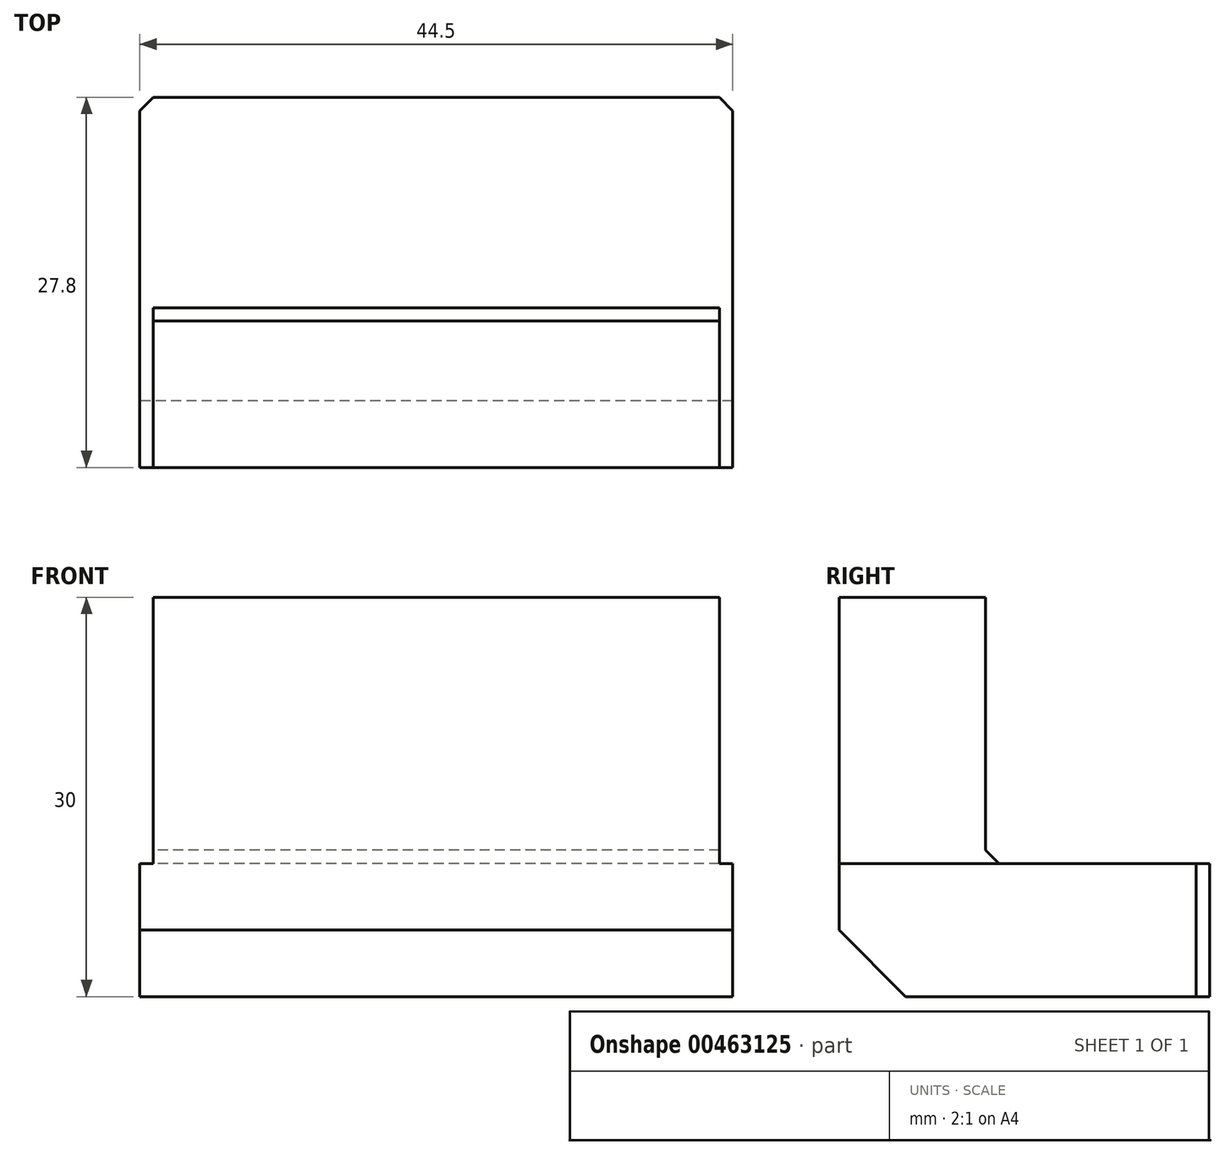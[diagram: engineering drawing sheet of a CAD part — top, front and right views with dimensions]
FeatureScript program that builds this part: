
annotation { "Feature Type Name" : "Feature", "Feature Type Description" : "" }
export const myFeature = defineFeature(function(context is Context, id is Id, definition is map)
    precondition{}
    {
        {
            var Q0;
            Q0=qCreatedBy(makeId("Top.planeOp"),FACE);
            var sketch = newSketch(context, id + "F0", { "sketchPlane" : qUnion([Q0])});
            skLineSegment(sketch, "E0.bottom", {"start": v(22.25, -13.9) * mm, "end": v(-22.25, -13.9) * mm});
            skLineSegment(sketch, "E0.top", {"start": v(22.25, 13.9) * mm, "end": v(-22.25, 13.9) * mm});
            skLineSegment(sketch, "E0.left", {"start": v(22.25, -13.9) * mm, "end": v(22.25, 13.9) * mm});
            skLineSegment(sketch, "E0.right", {"start": v(-22.25, -13.9) * mm, "end": v(-22.25, 13.9) * mm});
            skPoint(sketch, "E0.middle", {"position": v(0, 0) * mm});
            skLineSegment(sketch, "E1", {"start": v(-21.25, 13.9) * mm, "end": v(-21.25, -13.9) * mm});
            skLineSegment(sketch, "E2", {"start": v(21.25, 13.9) * mm, "end": v(21.25, -13.9) * mm});
            skLineSegment(sketch, "E3", {"start": v(-21.25, -2.9) * mm, "end": v(21.25, -2.9) * mm});
            skSolve(sketch);
        }
        {
            var Q0;
            Q0=makeQuery(id+"F0.imprint","IMPRINT",FACE,{"disambiguationData":[TD([[makeQuery(id+"F0.imprint","IMPRINT",EDGE,{"derivedFrom":sQuery(id+"F0.wireOp",EDGE,"E0.bottom")}),-1.0]])]});
            var Q1;
            {var subQ5=sQuery(id+"F0.wireOp",EDGE,"E3");Q1=makeQuery(id+"F0.imprint","IMPRINT",FACE,{"disambiguationData":[TD([[makeQuery(id+"F0.imprint","IMPRINT",EDGE,{"derivedFrom":subQ5}),1.0]])]});}
            var Q2;
            {var subQ4=sQuery(id+"F0.wireOp",EDGE,"E0.right");Q2=makeQuery(id+"F0.imprint","IMPRINT",FACE,{"disambiguationData":[TD([[makeQuery(id+"F0.imprint","IMPRINT",EDGE,{"derivedFrom":subQ4}),-1.0]])]});}
            var Q3;
            {var subQ0=sQuery(id+"F0.wireOp",EDGE,"E0.left");Q3=makeQuery(id+"F0.imprint","IMPRINT",FACE,{"disambiguationData":[TD([[makeQuery(id+"F0.imprint","IMPRINT",EDGE,{"derivedFrom":subQ0}),1.0]])]});}
            extrude(context, id + "F1", {"entities" : qUnion([Q0, Q1, Q2, Q3]), "oppositeDirection" : true, "depth" : 30 * mm});
        }
        {
            var Q0;
            {var subQ0=sQuery(id+"F0.wireOp",EDGE,"E0.right");Q0=makeQuery(id+"F0.imprint","IMPRINT",FACE,{"disambiguationData":[TD([[makeQuery(id+"F0.imprint","IMPRINT",EDGE,{"derivedFrom":subQ0}),-1.0]])]});}
            var Q1;
            {var subQ0=sQuery(id+"F0.wireOp",EDGE,"E0.left");Q1=makeQuery(id+"F0.imprint","IMPRINT",FACE,{"disambiguationData":[TD([[makeQuery(id+"F0.imprint","IMPRINT",EDGE,{"derivedFrom":subQ0}),1.0]])]});}
            extrude(context, id + "F2", {"entities" : qUnion([Q0, Q1]), "operationType" : NewBodyOperationType.REMOVE, "oppositeDirection" : true, "depth" : 20 * mm});
        }
        {
            var Q0;
            {var subQ5=sQuery(id+"F0.wireOp",EDGE,"E3");Q0=makeQuery(id+"F0.imprint","IMPRINT",FACE,{"disambiguationData":[TD([[makeQuery(id+"F0.imprint","IMPRINT",EDGE,{"derivedFrom":subQ5}),1.0]])]});}
            extrude(context, id + "F3", {"entities" : qUnion([Q0]), "operationType" : NewBodyOperationType.REMOVE, "oppositeDirection" : true, "depth" : 20 * mm});
        }
        {
            var Q0;
            Q0=makeQuery(id+"F1.opExtrude","CAP_EDGE",EDGE,{"disambiguationData":[OSD([sQuery(id+"F0.wireOp",EDGE,"E0.bottom")])],"isStart":false});
            var Q1;
            {var subQ0=sQuery(id+"F0.wireOp",EDGE,"E0.top");Q1=makeQuery(id+"F3.boolean.opBoolean","MERGE",EDGE,{"derivedFrom":[makeQuery(id+"F2.boolean.opBoolean","COPY",EDGE,{"derivedFrom":makeQuery(id+"F2.opExtrude","CAP_EDGE",EDGE,{"disambiguationData":[OSD([subQ0]),TDD([makeQuery(id+"F0.imprint","IMPRINT",EDGE,{"disambiguationData":[TD([[makeQuery(id+"F0.imprint","INTERSECT",VERTEX,{"derivedFrom":[subQ0,sQuery(id+"F0.wireOp",EDGE,"E0.left")]}),-1.0]])],"derivedFrom":subQ0})])],"isStart":false})}),makeQuery(id+"F2.boolean.opBoolean","COPY",EDGE,{"derivedFrom":makeQuery(id+"F2.opExtrude","CAP_EDGE",EDGE,{"disambiguationData":[OSD([subQ0]),TDD([makeQuery(id+"F0.imprint","IMPRINT",EDGE,{"disambiguationData":[TD([[makeQuery(id+"F0.imprint","INTERSECT",VERTEX,{"derivedFrom":[subQ0,sQuery(id+"F0.wireOp",EDGE,"E0.right")]}),1.0]])],"derivedFrom":subQ0})])],"isStart":false})}),makeQuery(id+"F3.opExtrude","CAP_EDGE",EDGE,{"disambiguationData":[OSD([subQ0])],"isStart":false})]});}
            chamfer(context, id + "F4", {"entities" : qUnion([Q0, Q1]), "width" : 5 * mm, "tangentPropagation" : true});
        }
        {
            var Q0;
            {var subQ0=sQuery(id+"F0.wireOp",EDGE,"E0.bottom");Q0=makeQuery(id+"F2.boolean.opBoolean","COPY",EDGE,{"derivedFrom":makeQuery(id+"F2.opExtrude","CAP_EDGE",EDGE,{"disambiguationData":[OSD([subQ0]),TDD([makeQuery(id+"F0.imprint","IMPRINT",EDGE,{"disambiguationData":[TD([[makeQuery(id+"F0.imprint","INTERSECT",VERTEX,{"derivedFrom":[subQ0,sQuery(id+"F0.wireOp",EDGE,"E0.right")]}),1.0]])],"derivedFrom":subQ0})])],"isStart":false})});}
            var Q1;
            {var subQ0=sQuery(id+"F0.wireOp",EDGE,"E0.bottom");Q1=makeQuery(id+"F2.boolean.opBoolean","COPY",EDGE,{"derivedFrom":makeQuery(id+"F2.opExtrude","CAP_EDGE",EDGE,{"disambiguationData":[OSD([subQ0]),TDD([makeQuery(id+"F0.imprint","IMPRINT",EDGE,{"disambiguationData":[TD([[makeQuery(id+"F0.imprint","INTERSECT",VERTEX,{"derivedFrom":[subQ0,sQuery(id+"F0.wireOp",EDGE,"E0.left")]}),-1.0]])],"derivedFrom":subQ0})])],"isStart":false})});}
            var Q2;
            Q2=makeQuery(id+"F3.boolean.opBoolean","COPY",EDGE,{"derivedFrom":makeQuery(id+"F3.opExtrude","CAP_EDGE",EDGE,{"disambiguationData":[OSD([sQuery(id+"F0.wireOp",EDGE,"E3")])],"isStart":false})});
            var Q3;
            Q3=makeQuery(id+"F2.boolean.opBoolean","COPY",EDGE,{"derivedFrom":makeQuery(id+"F2.opExtrude","SWEPT_EDGE",EDGE,{"disambiguationData":[OSD([sQuery(id+"F0.wireOp",EDGE,"E0.bottom"),sQuery(id+"F0.wireOp",EDGE,"E1")])]})});
            var Q4;
            Q4=makeQuery(id+"F2.boolean.opBoolean","COPY",EDGE,{"derivedFrom":makeQuery(id+"F2.opExtrude","SWEPT_EDGE",EDGE,{"disambiguationData":[OSD([sQuery(id+"F0.wireOp",EDGE,"E0.bottom"),sQuery(id+"F0.wireOp",EDGE,"E2")])]})});
            var Q5;
            Q5=makeQuery(id+"F3.boolean.opBoolean","COPY",EDGE,{"derivedFrom":makeQuery(id+"F3.opExtrude","SWEPT_EDGE",EDGE,{"disambiguationData":[OSD([sQuery(id+"F0.wireOp",EDGE,"E2"),sQuery(id+"F0.wireOp",EDGE,"E3")])]})});
            var Q6;
            Q6=makeQuery(id+"F3.boolean.opBoolean","COPY",EDGE,{"derivedFrom":makeQuery(id+"F3.opExtrude","SWEPT_EDGE",EDGE,{"disambiguationData":[OSD([sQuery(id+"F0.wireOp",EDGE,"E1"),sQuery(id+"F0.wireOp",EDGE,"E3")])]})});
            var Q7;
            Q7=makeQuery(id+"F1.opExtrude","SWEPT_EDGE",EDGE,{"disambiguationData":[OSD([sQuery(id+"F0.wireOp",EDGE,"E0.top"),sQuery(id+"F0.wireOp",EDGE,"E0.right")])]});
            var Q8;
            Q8=makeQuery(id+"F1.opExtrude","SWEPT_EDGE",EDGE,{"disambiguationData":[OSD([sQuery(id+"F0.wireOp",EDGE,"E0.top"),sQuery(id+"F0.wireOp",EDGE,"E0.left")])]});
            var Q9;
            {var subQ0=sQuery(id+"F0.wireOp",EDGE,"E2");var subQ1=sQuery(id+"F0.wireOp",EDGE,"E1");var subQ2=sQuery(id+"F0.wireOp",EDGE,"E0.top");var subQ3=sQuery(id+"F0.wireOp",EDGE,"E0.right");var subQ4=sQuery(id+"F0.wireOp",EDGE,"E0.bottom");var subQ5=sQuery(id+"F0.wireOp",EDGE,"E0.left");Q9=makeQuery(id+"F4.opChamfer","BLEND_EDGE",EDGE,{"blendedFrom":[makeQuery(id+"F3.boolean.opBoolean","MERGE",EDGE,{"derivedFrom":[makeQuery(id+"F2.boolean.opBoolean","COPY",EDGE,{"derivedFrom":makeQuery(id+"F2.opExtrude","CAP_EDGE",EDGE,{"disambiguationData":[OSD([subQ2]),TDD([makeQuery(id+"F0.imprint","IMPRINT",EDGE,{"disambiguationData":[TD([[makeQuery(id+"F0.imprint","INTERSECT",VERTEX,{"derivedFrom":[subQ2,subQ5]}),-1.0]])],"derivedFrom":subQ2})])],"isStart":false})}),makeQuery(id+"F2.boolean.opBoolean","COPY",EDGE,{"derivedFrom":makeQuery(id+"F2.opExtrude","CAP_EDGE",EDGE,{"disambiguationData":[OSD([subQ2]),TDD([makeQuery(id+"F0.imprint","IMPRINT",EDGE,{"disambiguationData":[TD([[makeQuery(id+"F0.imprint","INTERSECT",VERTEX,{"derivedFrom":[subQ2,subQ3]}),1.0]])],"derivedFrom":subQ2})])],"isStart":false})}),makeQuery(id+"F3.opExtrude","CAP_EDGE",EDGE,{"disambiguationData":[OSD([subQ2])],"isStart":false})]}),makeQuery(id+"F3.boolean.opBoolean","MERGE",FACE,{"derivedFrom":[makeQuery(id+"F2.boolean.opBoolean","COPY",FACE,{"derivedFrom":makeQuery(id+"F2.opExtrude","CAP_FACE",FACE,{"disambiguationData":[OSD([subQ4,subQ2,subQ5,subQ0])],"isStart":false})}),makeQuery(id+"F2.boolean.opBoolean","COPY",FACE,{"derivedFrom":makeQuery(id+"F2.opExtrude","CAP_FACE",FACE,{"disambiguationData":[OSD([subQ4,subQ2,subQ3,subQ1])],"isStart":false})}),makeQuery(id+"F3.opExtrude","CAP_FACE",FACE,{"disambiguationData":[OSD([subQ2,subQ1,subQ0,sQuery(id+"F0.wireOp",EDGE,"E3")])],"isStart":false})]})],"blendedInto":[makeQuery(id+"F3.boolean.opBoolean","MERGE",FACE,{"derivedFrom":[makeQuery(id+"F2.boolean.opBoolean","COPY",FACE,{"derivedFrom":makeQuery(id+"F2.opExtrude","CAP_FACE",FACE,{"disambiguationData":[OSD([subQ4,subQ2,subQ5,subQ0])],"isStart":false})}),makeQuery(id+"F2.boolean.opBoolean","COPY",FACE,{"derivedFrom":makeQuery(id+"F2.opExtrude","CAP_FACE",FACE,{"disambiguationData":[OSD([subQ4,subQ2,subQ3,subQ1])],"isStart":false})}),makeQuery(id+"F3.opExtrude","CAP_FACE",FACE,{"disambiguationData":[OSD([subQ2,subQ1,subQ0,sQuery(id+"F0.wireOp",EDGE,"E3")])],"isStart":false})]})]});}
            var Q10;
            {var subQ0=sQuery(id+"F0.wireOp",EDGE,"E0.top");Q10=makeQuery(id+"F4.opChamfer","BLEND_EDGE",EDGE,{"blendedFrom":[makeQuery(id+"F3.boolean.opBoolean","MERGE",EDGE,{"derivedFrom":[makeQuery(id+"F2.boolean.opBoolean","COPY",EDGE,{"derivedFrom":makeQuery(id+"F2.opExtrude","CAP_EDGE",EDGE,{"disambiguationData":[OSD([subQ0]),TDD([makeQuery(id+"F0.imprint","IMPRINT",EDGE,{"disambiguationData":[TD([[makeQuery(id+"F0.imprint","INTERSECT",VERTEX,{"derivedFrom":[subQ0,sQuery(id+"F0.wireOp",EDGE,"E0.left")]}),-1.0]])],"derivedFrom":subQ0})])],"isStart":false})}),makeQuery(id+"F2.boolean.opBoolean","COPY",EDGE,{"derivedFrom":makeQuery(id+"F2.opExtrude","CAP_EDGE",EDGE,{"disambiguationData":[OSD([subQ0]),TDD([makeQuery(id+"F0.imprint","IMPRINT",EDGE,{"disambiguationData":[TD([[makeQuery(id+"F0.imprint","INTERSECT",VERTEX,{"derivedFrom":[subQ0,sQuery(id+"F0.wireOp",EDGE,"E0.right")]}),1.0]])],"derivedFrom":subQ0})])],"isStart":false})}),makeQuery(id+"F3.opExtrude","CAP_EDGE",EDGE,{"disambiguationData":[OSD([subQ0])],"isStart":false})]}),makeQuery(id+"F1.opExtrude","SWEPT_FACE",FACE,{"disambiguationData":[OSD([subQ0])]})],"blendedInto":[makeQuery(id+"F1.opExtrude","SWEPT_FACE",FACE,{"disambiguationData":[OSD([subQ0])]})]});}
            chamfer(context, id + "F5", {"entities" : qUnion([Q0, Q1, Q2, Q3, Q4, Q5, Q6, Q7, Q8, Q9, Q10]), "width" : 1 * mm, "tangentPropagation" : true});
        }
    });
